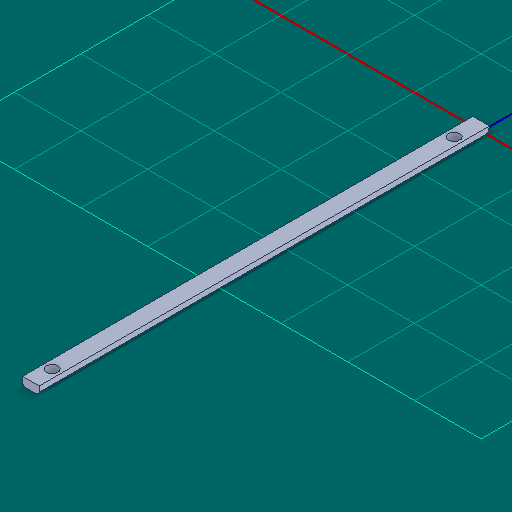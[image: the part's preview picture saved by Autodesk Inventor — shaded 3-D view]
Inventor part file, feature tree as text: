
AUTODESK INVENTOR PART (.ipt)
format: ipt  version: 2025 (Build 290162000, 162)  size: 210,432 bytes
history: native  units: in
note: dims shown in document units (in); Inventor stores cm internally (conversion verified against a paired STEP export)
features: extrude x5, sketch x5, thicken_offset x1, projected_geometry x1, other x1
ambient origin geometry x8: Origin, YZ Plane, XZ Plane, XY Plane, X Axis, Y Axis, Z Axis, Center Point
bodies: Solid1 (feature_tree)
feature tree (13):
  extrude  "Extrusion1"  Depth=12.1875in
  thicken_offset  "Thicken1"
  extrude  "Extrusion2"  Depth=17.125in
  extrude  "Extrusion3"  Depth=6.0268in
  extrude  "Extrusion4"  Depth=0.25in TaperAngle=0.0deg
  extrude  "Extrusion5"  Depth=0.125in TaperAngle=0.0deg
  sketch  "Sketch2"  dims[d0=0.0625in d1=0.0in d2=12.1875in]
  sketch  "Sketch3"  dims[d3=12.125in d4=17.125in]
  sketch  "Sketch4"  dims[d5=0.0in d6=6.0268in]
  sketch  "Sketch5"  dims[d8=0.25in d9=1.0in d10=0.0in]
  projected_geometry  "Projected Loop1"
  sketch  "Sketch6"  dims[d11=0.25in d12=0.0in d13=0.125in d14=0.0in]
  other  "Cut-Revolve3"
